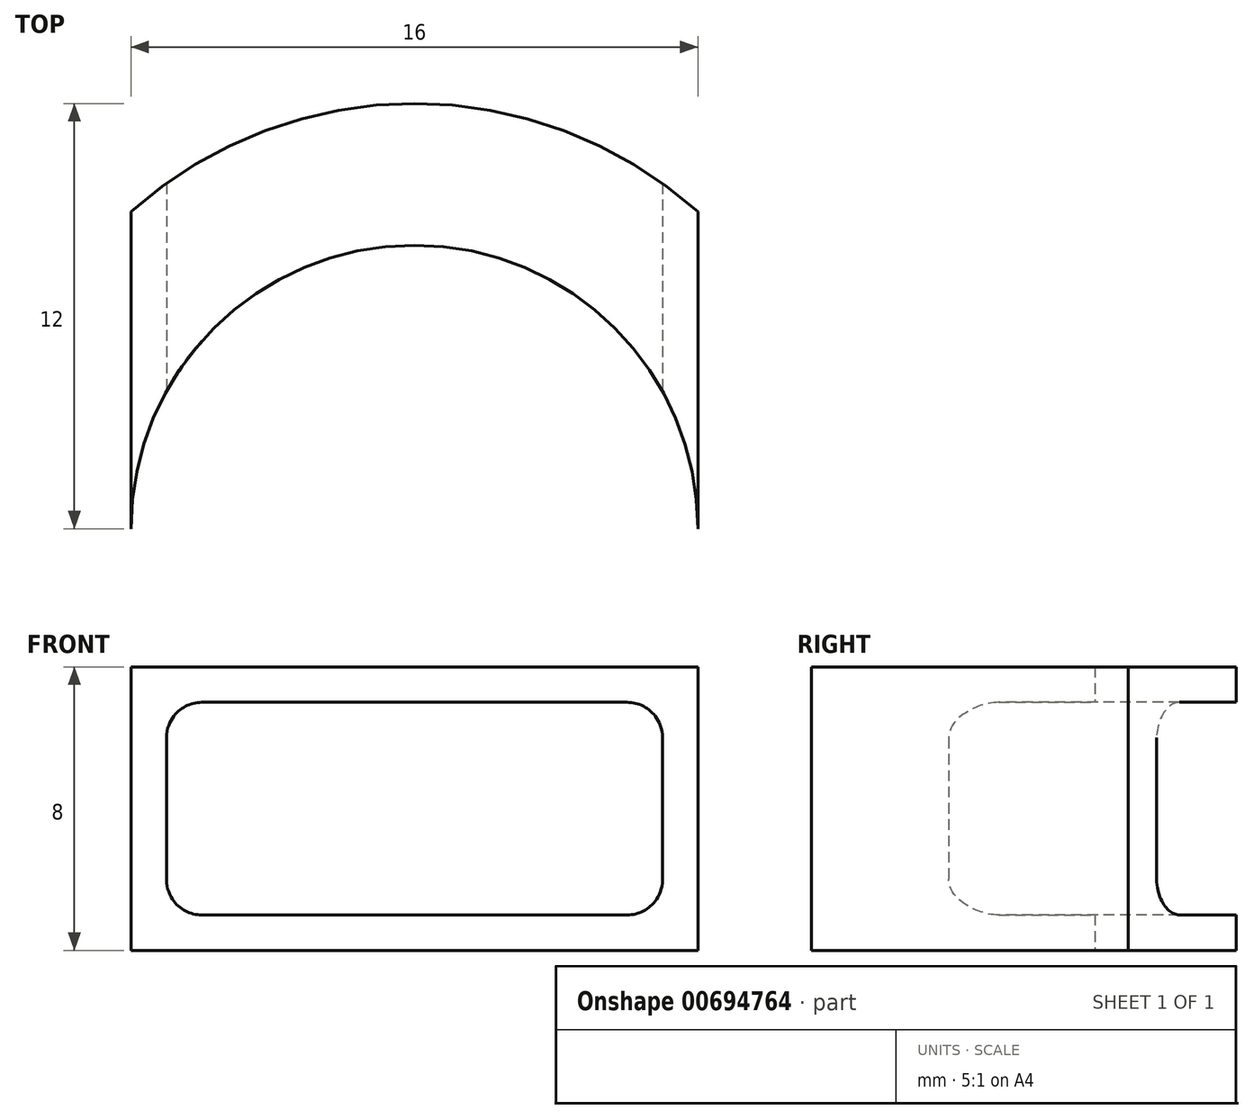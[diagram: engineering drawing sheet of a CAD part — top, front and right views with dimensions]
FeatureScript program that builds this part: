
annotation { "Feature Type Name" : "Feature", "Feature Type Description" : "" }
export const myFeature = defineFeature(function(context is Context, id is Id, definition is map)
    precondition{}
    {
        {
            var Q0;
            Q0=qCreatedBy(makeId("Top.planeOp"),FACE);
            var sketch = newSketch(context, id + "F0", { "sketchPlane" : qUnion([Q0])});
            skArc(sketch, "E0", {"start": v(8, 8.94) * mm, "mid": v(0, 12) * mm, "end": v(-8, 8.94) * mm});
            skArc(sketch, "E1", {"start": v(8, 0) * mm, "mid": v(0, 8) * mm, "end": v(-8, 0) * mm});
            skLineSegment(sketch, "E2.left", {"start": v(-8, 8.94) * mm, "end": v(-8, 0) * mm});
            skLineSegment(sketch, "E2.right", {"start": v(8, 8.94) * mm, "end": v(8, 0) * mm});
            skPoint(sketch, "E3.orphan", {"position": v(8, 13) * mm});
            skSolve(sketch);
        }
        {
            var Q0;
            Q0=makeQuery(id+"F0.imprint","IMPRINT",FACE,{"disambiguationData":[TD([[makeQuery(id+"F0.imprint","IMPRINT",EDGE,{"derivedFrom":sQuery(id+"F0.wireOp",EDGE,"E0")}),1.0]])]});
            extrude(context, id + "F1", {"entities" : qUnion([Q0]), "depth" : 4 * mm, "offsetDistance" : 25 * mm, "hasSecondDirection" : true, "secondDirectionOppositeDirection" : true, "secondDirectionDepth" : 4 * mm});
        }
        {
            var Q0;
            Q0=qCreatedBy(makeId("Front.planeOp"),FACE);
            var sketch = newSketch(context, id + "F2", { "sketchPlane" : qUnion([Q0])});
            skLineSegment(sketch, "E4.bottom", {"start": v(-7, 3) * mm, "end": v(7, 3) * mm});
            skLineSegment(sketch, "E4.top", {"start": v(-7, -3) * mm, "end": v(7, -3) * mm});
            skLineSegment(sketch, "E4.left", {"start": v(-7, 3) * mm, "end": v(-7, -3) * mm});
            skLineSegment(sketch, "E4.right", {"start": v(7, 3) * mm, "end": v(7, -3) * mm});
            skSolve(sketch);
        }
        {
            var Q0;
            Q0 = qSketchRegion(id + "F2", true);
            extrude(context, id + "F3", {"entities" : qUnion([Q0]), "operationType" : NewBodyOperationType.REMOVE, "oppositeDirection" : true, "depth" : 25 * mm, "offsetDistance" : 25 * mm});
        }
        {
            var Q0;
            Q0=makeQuery(id+"F3.boolean.opBoolean","COPY",EDGE,{"derivedFrom":makeQuery(id+"F3.opExtrude","SWEPT_EDGE",EDGE,{"disambiguationData":[OSD([sQuery(id+"F2.wireOp",EDGE,"E4.bottom"),sQuery(id+"F2.wireOp",EDGE,"E4.left")])]})});
            var Q1;
            Q1=makeQuery(id+"F3.boolean.opBoolean","COPY",EDGE,{"derivedFrom":makeQuery(id+"F3.opExtrude","SWEPT_EDGE",EDGE,{"disambiguationData":[OSD([sQuery(id+"F2.wireOp",EDGE,"E4.top"),sQuery(id+"F2.wireOp",EDGE,"E4.left")])]})});
            var Q2;
            Q2=makeQuery(id+"F3.boolean.opBoolean","COPY",EDGE,{"derivedFrom":makeQuery(id+"F3.opExtrude","SWEPT_EDGE",EDGE,{"disambiguationData":[OSD([sQuery(id+"F2.wireOp",EDGE,"E4.top"),sQuery(id+"F2.wireOp",EDGE,"E4.right")])]})});
            var Q3;
            Q3=makeQuery(id+"F3.boolean.opBoolean","COPY",EDGE,{"derivedFrom":makeQuery(id+"F3.opExtrude","SWEPT_EDGE",EDGE,{"disambiguationData":[OSD([sQuery(id+"F2.wireOp",EDGE,"E4.bottom"),sQuery(id+"F2.wireOp",EDGE,"E4.right")])]})});
            fillet(context, id + "F4", {"entities" : qUnion([Q0, Q1, Q2, Q3]), "radius" : 1 * mm, "tangentPropagation" : true, "allowEdgeOverflow" : false});
        }
    });
